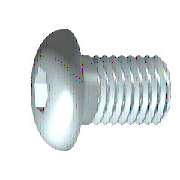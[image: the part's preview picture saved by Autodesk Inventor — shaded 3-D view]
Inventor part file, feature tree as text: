
AUTODESK INVENTOR PART (.ipt)
format: ipt  version: 2023.5 (Build 275446000, 446)  size: 188,928 bytes
history: native  units: mm (DEFAULTED — no unit token found)
features: extrude x1, plane x1, fillet x1
ambient origin geometry x7: Origin, YZ Plane, XY Plane, X Axis, Y Axis, Z Axis, Center Point
bodies: Solid1 (feature_tree), Body (feature_tree)
feature tree (3):
  extrude  "Slot"  Depth=23.812246mm
  plane  "Work Plane1"
  fillet  "Fillet2"  Radius=1.5876mm
